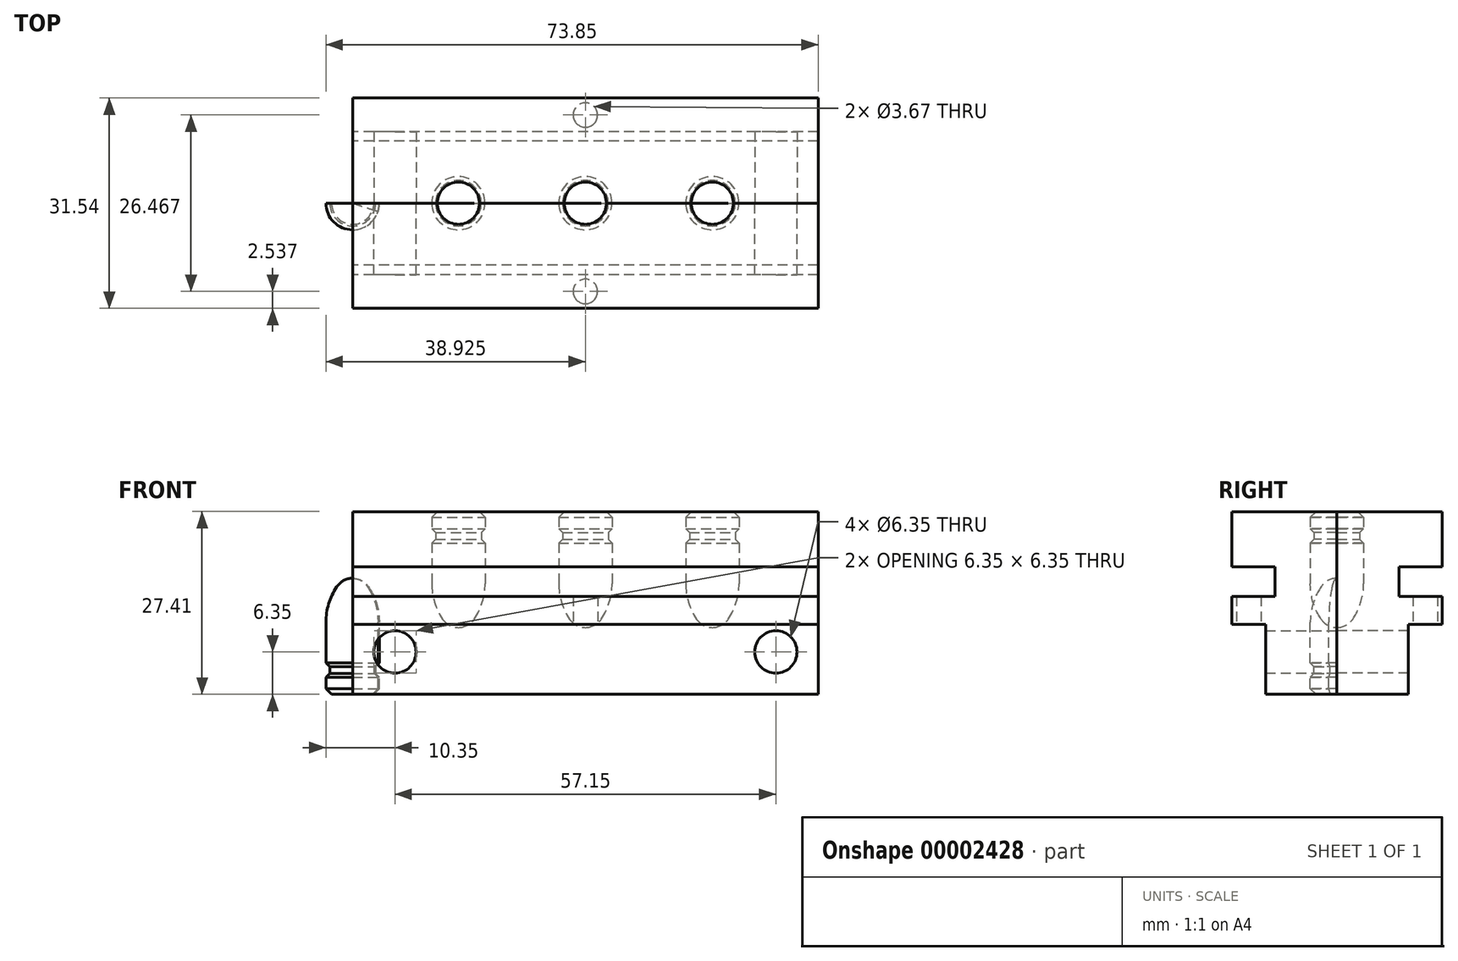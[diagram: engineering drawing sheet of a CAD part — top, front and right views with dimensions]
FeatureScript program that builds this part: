
annotation { "Feature Type Name" : "Feature", "Feature Type Description" : "" }
export const myFeature = defineFeature(function(context is Context, id is Id, definition is map)
    precondition{}
    {
        {
            var Q0;
            Q0=qCreatedBy(makeId("Front.planeOp"),FACE);
            var sketch = newSketch(context, id + "F0", { "sketchPlane" : qUnion([Q0])});
            skLineSegment(sketch, "E0", {"start": v(0, 0) * mm, "end": v(3.16, 0) * mm});
            skLineSegment(sketch, "E1", {"start": v(4, 0.84) * mm, "end": v(4, 2.54) * mm});
            skArc(sketch, "E2", {"start": v(4, 10.8) * mm, "mid": v(3.59, 13.58) * mm, "end": v(2.38, 16.13) * mm});
            skArc(sketch, "E3", {"start": v(2.38, 16.13) * mm, "mid": v(1.35, 17.06) * mm, "end": v(0, 17.4) * mm});
            skLineSegment(sketch, "E4", {"start": v(0, 17.4) * mm, "end": v(0, 0) * mm});
            skLineSegment(sketch, "E5.trimOffspring", {"start": v(4, 4.7) * mm, "end": v(4, 10.8) * mm});
            skLineSegment(sketch, "E6", {"start": v(4, 4.7) * mm, "end": v(3.43, 4.13) * mm});
            skLineSegment(sketch, "E7", {"start": v(3.43, 4.13) * mm, "end": v(3.43, 3.11) * mm});
            skLineSegment(sketch, "E8", {"start": v(3.43, 3.11) * mm, "end": v(4, 2.54) * mm});
            skLineSegment(sketch, "E9", {"start": v(4, 0.84) * mm, "end": v(3.16, 0) * mm});
            skSolve(sketch);
        }
        {
            var Q0;
            Q0=makeQuery(id+"F0.imprint","IMPRINT",FACE,{"disambiguationData":[TD([[makeQuery(id+"F0.imprint","IMPRINT",EDGE,{"derivedFrom":sQuery(id+"F0.wireOp",EDGE,"E0")}),1.0]])]});
            var Q1;
            Q1=sQuery(id+"F0.wireOp",EDGE,"E4");
            revolve(context, id + "F1", {"entities" : qUnion([Q0]), "axis" : qUnion([Q1]), "revolveType" : RevolveType.FULL});
        }
        {
            var Q0;
            Q0=qCreatedBy(makeId("Right.planeOp"),FACE);
            var sketch = newSketch(context, id + "F2", { "sketchPlane" : qUnion([Q0])});
            skLineSegment(sketch, "E10", {"start": v(0, 0) * mm, "end": v(0, 27.4) * mm});
            skLineSegment(sketch, "E11", {"start": v(0, 27.4) * mm, "end": v(15.77, 27.4) * mm});
            skLineSegment(sketch, "E12", {"start": v(15.77, 27.4) * mm, "end": v(15.77, 19.15) * mm});
            skLineSegment(sketch, "E13", {"start": v(15.77, 19.15) * mm, "end": v(9.3, 19.15) * mm});
            skLineSegment(sketch, "E14", {"start": v(9.3, 19.15) * mm, "end": v(9.3, 14.7) * mm});
            skLineSegment(sketch, "E15", {"start": v(9.3, 14.7) * mm, "end": v(15.77, 14.7) * mm});
            skLineSegment(sketch, "E16", {"start": v(15.77, 14.7) * mm, "end": v(15.77, 10.52) * mm});
            skLineSegment(sketch, "E17", {"start": v(15.77, 10.52) * mm, "end": v(10.72, 10.52) * mm});
            skLineSegment(sketch, "E18", {"start": v(10.72, 10.52) * mm, "end": v(10.72, 0) * mm});
            skLineSegment(sketch, "E19", {"start": v(10.72, 0) * mm, "end": v(0, 0) * mm});
            skSolve(sketch);
        }
        {
            var Q0;
            Q0=qSketchRegion(id+"F2",true);
            extrude(context, id + "F3", {"entities" : qUnion([Q0]), "depth" : 69.85 * mm});
        }
        {
            var Q0;
            Q0=makeQuery(id+"F1.opRevolve","SWEPT_BODY",BODY,{"disambiguationData":[OSD([sQuery(id+"F0.wireOp",EDGE,"E0"),sQuery(id+"F0.wireOp",EDGE,"E1"),sQuery(id+"F0.wireOp",EDGE,"E2"),sQuery(id+"F0.wireOp",EDGE,"E3"),sQuery(id+"F0.wireOp",EDGE,"E4"),sQuery(id+"F0.wireOp",EDGE,"E5.trimOffspring"),sQuery(id+"F0.wireOp",EDGE,"E6"),sQuery(id+"F0.wireOp",EDGE,"E7"),sQuery(id+"F0.wireOp",EDGE,"E8"),sQuery(id+"F0.wireOp",EDGE,"E9")])]});
            var Q1;
            Q1=makeQuery(id+"F3.opExtrude","SWEPT_EDGE",EDGE,{"disambiguationData":[OSD([sQuery(id+"F2.wireOp",EDGE,"E10"),sQuery(id+"F2.wireOp",EDGE,"E19")])]});
            transform(context, id + "F4", {"entities" : qUnion([Q0]), "transformType" : TransformType.ROTATION, "transformAxis" : qUnion([Q1]), "angle" : 180 * degree, "oppositeX" : false, "oppositeY" : false, "oppositeZ" : false, "makeCopy" : false});
        }
        {
            var Q0;
            Q0=makeQuery(id+"F1.opRevolve","SWEPT_BODY",BODY,{"disambiguationData":[OSD([sQuery(id+"F0.wireOp",EDGE,"E0"),sQuery(id+"F0.wireOp",EDGE,"E1"),sQuery(id+"F0.wireOp",EDGE,"E2"),sQuery(id+"F0.wireOp",EDGE,"E3"),sQuery(id+"F0.wireOp",EDGE,"E4"),sQuery(id+"F0.wireOp",EDGE,"E5.trimOffspring"),sQuery(id+"F0.wireOp",EDGE,"E6"),sQuery(id+"F0.wireOp",EDGE,"E7"),sQuery(id+"F0.wireOp",EDGE,"E8"),sQuery(id+"F0.wireOp",EDGE,"E9")])]});
            var Q1;
            Q1=makeQuery(id+"F3.opExtrude","CAP_EDGE",EDGE,{"disambiguationData":[OSD([sQuery(id+"F2.wireOp",EDGE,"E10")])],"isStart":true});
            transform(context, id + "F5", {"entities" : qUnion([Q0]), "transformType" : TransformType.TRANSLATION_ENTITY, "oppositeDirectionEntity" : false, "transformLine" : qUnion([Q1]), "oppositeX" : false, "oppositeY" : false, "oppositeZ" : false, "makeCopy" : false});
        }
        {
            var Q0;
            Q0=makeQuery(id+"F1.opRevolve","SWEPT_BODY",BODY,{"disambiguationData":[OSD([sQuery(id+"F0.wireOp",EDGE,"E0"),sQuery(id+"F0.wireOp",EDGE,"E1"),sQuery(id+"F0.wireOp",EDGE,"E2"),sQuery(id+"F0.wireOp",EDGE,"E3"),sQuery(id+"F0.wireOp",EDGE,"E4"),sQuery(id+"F0.wireOp",EDGE,"E5.trimOffspring"),sQuery(id+"F0.wireOp",EDGE,"E6"),sQuery(id+"F0.wireOp",EDGE,"E7"),sQuery(id+"F0.wireOp",EDGE,"E8"),sQuery(id+"F0.wireOp",EDGE,"E9")])]});
            transform(context, id + "F6", {"entities" : qUnion([Q0]), "transformType" : TransformType.TRANSLATION_3D, "dx" : 15.88 * mm, "dy" : 0 * mm, "dz" : 0 * mm, "makeCopy" : true});
        }
        {
            var Q0;
            Q0=makeQuery(id+"F1.opRevolve","SWEPT_BODY",BODY,{"disambiguationData":[OSD([sQuery(id+"F0.wireOp",EDGE,"E0"),sQuery(id+"F0.wireOp",EDGE,"E1"),sQuery(id+"F0.wireOp",EDGE,"E2"),sQuery(id+"F0.wireOp",EDGE,"E3"),sQuery(id+"F0.wireOp",EDGE,"E4"),sQuery(id+"F0.wireOp",EDGE,"E5.trimOffspring"),sQuery(id+"F0.wireOp",EDGE,"E6"),sQuery(id+"F0.wireOp",EDGE,"E7"),sQuery(id+"F0.wireOp",EDGE,"E8"),sQuery(id+"F0.wireOp",EDGE,"E9")])]});
            transform(context, id + "F7", {"entities" : qUnion([Q0]), "transformType" : TransformType.TRANSLATION_3D, "dx" : 34.92 * mm, "dy" : 0 * mm, "dz" : 0 * mm, "makeCopy" : true});
        }
        {
            var Q0;
            Q0=makeQuery(id+"F1.opRevolve","SWEPT_BODY",BODY,{"disambiguationData":[OSD([sQuery(id+"F0.wireOp",EDGE,"E0"),sQuery(id+"F0.wireOp",EDGE,"E1"),sQuery(id+"F0.wireOp",EDGE,"E2"),sQuery(id+"F0.wireOp",EDGE,"E3"),sQuery(id+"F0.wireOp",EDGE,"E4"),sQuery(id+"F0.wireOp",EDGE,"E5.trimOffspring"),sQuery(id+"F0.wireOp",EDGE,"E6"),sQuery(id+"F0.wireOp",EDGE,"E7"),sQuery(id+"F0.wireOp",EDGE,"E8"),sQuery(id+"F0.wireOp",EDGE,"E9")])]});
            transform(context, id + "F8", {"entities" : qUnion([Q0]), "transformType" : TransformType.TRANSLATION_3D, "dx" : 53.97 * mm, "dy" : 0 * mm, "dz" : 0 * mm, "makeCopy" : false});
        }
        {
            var Q0;
            Q0=qCreatedBy(makeId("Front.planeOp"),FACE);
            var sketch = newSketch(context, id + "F9", { "sketchPlane" : qUnion([Q0])});
            skCircle(sketch, "E20", {"center": v(6.35, 6.35) * mm, "radius": 3.18 * mm});
            skCircle(sketch, "E21", {"center": v(63.5, 6.35) * mm, "radius": 3.18 * mm});
            skSolve(sketch);
        }
        {
            var Q0;
            Q0=qSketchRegion(id+"F9",true);
            extrude(context, id + "F10", {"entities" : qUnion([Q0]), "operationType" : NewBodyOperationType.REMOVE, "oppositeDirection" : true, "depth" : 25.4 * mm});
        }
        {
            var Q0;
            Q0=qCreatedBy(makeId("Top.planeOp"),FACE);
            var sketch = newSketch(context, id + "F11", { "sketchPlane" : qUnion([Q0])});
            skCircle(sketch, "E22", {"center": v(34.93, 13.23) * mm, "radius": 1.83 * mm});
            skSolve(sketch);
        }
        {
            var Q0;
            Q0=qSketchRegion(id+"F11",true);
            extrude(context, id + "F12", {"entities" : qUnion([Q0]), "operationType" : NewBodyOperationType.REMOVE, "depth" : 16.65 * mm});
        }
        {
            var Q0;
            Q0=makeQuery(id+"F1.opRevolve","SWEPT_BODY",BODY,{"disambiguationData":[OSD([sQuery(id+"F0.wireOp",EDGE,"E0"),sQuery(id+"F0.wireOp",EDGE,"E1"),sQuery(id+"F0.wireOp",EDGE,"E2"),sQuery(id+"F0.wireOp",EDGE,"E3"),sQuery(id+"F0.wireOp",EDGE,"E4"),sQuery(id+"F0.wireOp",EDGE,"E5.trimOffspring"),sQuery(id+"F0.wireOp",EDGE,"E6"),sQuery(id+"F0.wireOp",EDGE,"E7"),sQuery(id+"F0.wireOp",EDGE,"E8"),sQuery(id+"F0.wireOp",EDGE,"E9")])]});
            var Q1;
            Q1=makeQuery(id+"F6.opPattern","COPY",BODY,{"derivedFrom":makeQuery(id+"F1.opRevolve","SWEPT_BODY",BODY,{"disambiguationData":[OSD([sQuery(id+"F0.wireOp",EDGE,"E0"),sQuery(id+"F0.wireOp",EDGE,"E1"),sQuery(id+"F0.wireOp",EDGE,"E2"),sQuery(id+"F0.wireOp",EDGE,"E3"),sQuery(id+"F0.wireOp",EDGE,"E4"),sQuery(id+"F0.wireOp",EDGE,"E5.trimOffspring"),sQuery(id+"F0.wireOp",EDGE,"E6"),sQuery(id+"F0.wireOp",EDGE,"E7"),sQuery(id+"F0.wireOp",EDGE,"E8"),sQuery(id+"F0.wireOp",EDGE,"E9")])]}),"instanceName":"1"});
            var Q2;
            Q2=makeQuery(id+"F7.opPattern","COPY",BODY,{"derivedFrom":makeQuery(id+"F1.opRevolve","SWEPT_BODY",BODY,{"disambiguationData":[OSD([sQuery(id+"F0.wireOp",EDGE,"E0"),sQuery(id+"F0.wireOp",EDGE,"E1"),sQuery(id+"F0.wireOp",EDGE,"E2"),sQuery(id+"F0.wireOp",EDGE,"E3"),sQuery(id+"F0.wireOp",EDGE,"E4"),sQuery(id+"F0.wireOp",EDGE,"E5.trimOffspring"),sQuery(id+"F0.wireOp",EDGE,"E6"),sQuery(id+"F0.wireOp",EDGE,"E7"),sQuery(id+"F0.wireOp",EDGE,"E8"),sQuery(id+"F0.wireOp",EDGE,"E9")])]}),"instanceName":"1"});
            var Q3;
            Q3=makeQuery(id+"F3.opExtrude","SWEPT_BODY",BODY,{"disambiguationData":[OSD([sQuery(id+"F2.wireOp",EDGE,"E10"),sQuery(id+"F2.wireOp",EDGE,"E11"),sQuery(id+"F2.wireOp",EDGE,"E12"),sQuery(id+"F2.wireOp",EDGE,"E13"),sQuery(id+"F2.wireOp",EDGE,"E14"),sQuery(id+"F2.wireOp",EDGE,"E15"),sQuery(id+"F2.wireOp",EDGE,"E16"),sQuery(id+"F2.wireOp",EDGE,"E17"),sQuery(id+"F2.wireOp",EDGE,"E18"),sQuery(id+"F2.wireOp",EDGE,"E19")])]});
            booleanBodies(context, id + "F13", {"operationType" : BooleanOperationType.SUBTRACTION, "tools" : qUnion([Q0, Q1, Q2]), "targets" : qUnion([Q3])});
        }
        {
            var Q0;
            Q0=makeQuery(id+"F3.opExtrude","SWEPT_BODY",BODY,{"disambiguationData":[OSD([sQuery(id+"F2.wireOp",EDGE,"E10"),sQuery(id+"F2.wireOp",EDGE,"E11"),sQuery(id+"F2.wireOp",EDGE,"E12"),sQuery(id+"F2.wireOp",EDGE,"E13"),sQuery(id+"F2.wireOp",EDGE,"E14"),sQuery(id+"F2.wireOp",EDGE,"E15"),sQuery(id+"F2.wireOp",EDGE,"E16"),sQuery(id+"F2.wireOp",EDGE,"E17"),sQuery(id+"F2.wireOp",EDGE,"E18"),sQuery(id+"F2.wireOp",EDGE,"E19")])]});
            var Q1;
            Q1=qCreatedBy(makeId("Front.planeOp"),FACE);
            mirror(context, id + "F14", {"entities" : qUnion([Q0]), "mirrorPlane" : qUnion([Q1])});
        }
        {
            var Q0;
            Q0=qSketchRegion(id+"F0",true);
            var Q1;
            Q1=sQuery(id+"F0.wireOp",EDGE,"E4");
            revolve(context, id + "F15", {"entities" : qUnion([Q0]), "axis" : qUnion([Q1]), "revolveType" : RevolveType.ONE_DIRECTION, "angle" : 180 * degree});
        }
        {
            var Q0;
            Q0=qCreatedBy(makeId("Top.planeOp"),FACE);
            var sketch = newSketch(context, id + "F16", { "sketchPlane" : qUnion([Q0])});
            skLineSegment(sketch, "E23", {"start": v(-1.13, -7.14) * mm, "end": v(0, 0) * mm});
            skLineSegment(sketch, "E24.0", {"start": v(0, 0) * mm, "end": v(3.16, 0) * mm});
            skSolve(sketch);
        }
        {
            var Q0;
            Q0=makeQuery(id+"F0.imprint","IMPRINT",FACE,{"disambiguationData":[TD([[makeQuery(id+"F0.imprint","IMPRINT",EDGE,{"derivedFrom":sQuery(id+"F0.wireOp",EDGE,"E0")}),1.0]])]});
            var sketch = newSketch(context, id + "F17", { "sketchPlane" : qUnion([Q0])});
            skArc(sketch, "E25.0", {"start": v(2.38, 16.13) * mm, "mid": v(1.35, 17.06) * mm, "end": v(0, 17.4) * mm});
            skArc(sketch, "E26.0", {"start": v(4, 10.8) * mm, "mid": v(3.59, 13.58) * mm, "end": v(2.38, 16.13) * mm});
            skLineSegment(sketch, "E27.0", {"start": v(4, 4.7) * mm, "end": v(4, 10.8) * mm});
            skLineSegment(sketch, "E28.0", {"start": v(4, 4.7) * mm, "end": v(3.43, 4.13) * mm});
            skLineSegment(sketch, "E29.0", {"start": v(3.43, 4.13) * mm, "end": v(3.43, 3.11) * mm});
            skLineSegment(sketch, "E30.0", {"start": v(3.43, 3.11) * mm, "end": v(4, 2.54) * mm});
            skLineSegment(sketch, "E31.0", {"start": v(4, 0.84) * mm, "end": v(4, 2.54) * mm});
            skLineSegment(sketch, "E32.0", {"start": v(4, 0.84) * mm, "end": v(3.16, 0) * mm});
            skLineSegment(sketch, "E33.0", {"start": v(0, 0) * mm, "end": v(3.16, 0) * mm});
            skLineSegment(sketch, "E34", {"start": v(0, 0) * mm, "end": v(0, -1.18) * mm});
            skLineSegment(sketch, "E35", {"start": v(0, -1.18) * mm, "end": v(5.3, -1.18) * mm});
            skLineSegment(sketch, "E36", {"start": v(5.3, -1.18) * mm, "end": v(5.3, 20.02) * mm});
            skLineSegment(sketch, "E37", {"start": v(5.3, 20.02) * mm, "end": v(0, 20.02) * mm});
            skLineSegment(sketch, "E38", {"start": v(0, 20.02) * mm, "end": v(0, 17.4) * mm});
            skSolve(sketch);
        }
        {
            var Q0;
            Q0=makeQuery(id+"F17.imprint","IMPRINT",FACE,{"disambiguationData":[TD([[makeQuery(id+"F17.imprint","IMPRINT",EDGE,{"derivedFrom":sQuery(id+"F17.wireOp",EDGE,"E25.0")}),-1.0]])]});
            var Q1;
            Q1=sQuery(id+"F16.wireOp",EDGE,"E23");
            sweep(context, id + "F18", {"profiles" : qUnion([Q0]), "path" : qUnion([Q1])});
        }
        {
            var Q0;
            Q0=makeQuery(id+"F18.opSweep","SWEPT_BODY",BODY,{"disambiguationData":[OSD([sQuery(id+"F16.wireOp",EDGE,"E23"),sQuery(id+"F17.wireOp",EDGE,"E25.0"),sQuery(id+"F17.wireOp",EDGE,"E26.0"),sQuery(id+"F17.wireOp",EDGE,"E27.0"),sQuery(id+"F17.wireOp",EDGE,"E28.0"),sQuery(id+"F17.wireOp",EDGE,"E29.0"),sQuery(id+"F17.wireOp",EDGE,"E30.0"),sQuery(id+"F17.wireOp",EDGE,"E31.0"),sQuery(id+"F17.wireOp",EDGE,"E32.0"),sQuery(id+"F17.wireOp",EDGE,"E33.0"),sQuery(id+"F17.wireOp",EDGE,"E34"),sQuery(id+"F17.wireOp",EDGE,"E35"),sQuery(id+"F17.wireOp",EDGE,"E36"),sQuery(id+"F17.wireOp",EDGE,"E37"),sQuery(id+"F17.wireOp",EDGE,"E38")])]});
            var Q1;
            Q1=makeQuery(id+"F15.opRevolve","SWEPT_BODY",BODY,{"disambiguationData":[OSD([sQuery(id+"F0.wireOp",EDGE,"E0"),sQuery(id+"F0.wireOp",EDGE,"E1"),sQuery(id+"F0.wireOp",EDGE,"E2"),sQuery(id+"F0.wireOp",EDGE,"E3"),sQuery(id+"F0.wireOp",EDGE,"E4"),sQuery(id+"F0.wireOp",EDGE,"E5.trimOffspring"),sQuery(id+"F0.wireOp",EDGE,"E6"),sQuery(id+"F0.wireOp",EDGE,"E7"),sQuery(id+"F0.wireOp",EDGE,"E8"),sQuery(id+"F0.wireOp",EDGE,"E9")])]});
            booleanBodies(context, id + "F19", {"operationType" : BooleanOperationType.SUBTRACTION, "tools" : qUnion([Q0]), "targets" : qUnion([Q1])});
        }
    });
